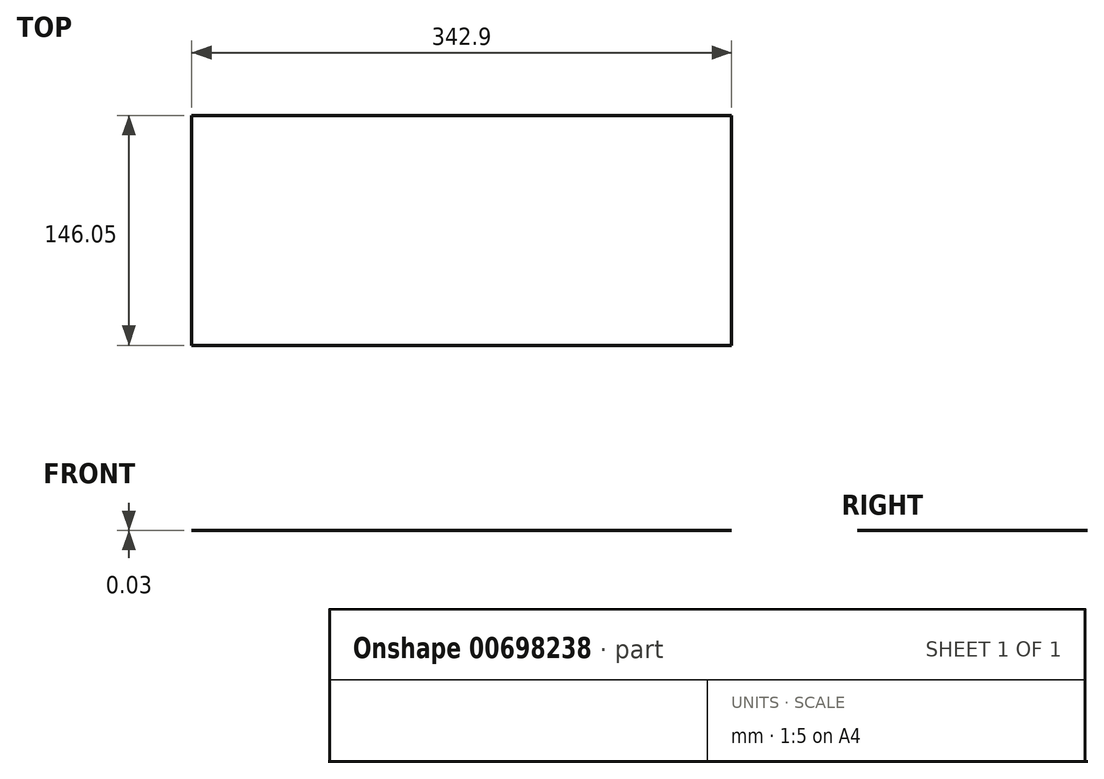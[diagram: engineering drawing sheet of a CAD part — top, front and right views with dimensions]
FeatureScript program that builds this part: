
annotation { "Feature Type Name" : "Feature", "Feature Type Description" : "" }
export const myFeature = defineFeature(function(context is Context, id is Id, definition is map)
    precondition{}
    {
        {
            var Q0;
            Q0=qCreatedBy(makeId("Top.planeOp"),FACE);
            var sketch = newSketch(context, id + "F0", { "sketchPlane" : qUnion([Q0])});
            skLineSegment(sketch, "E0.bottom", {"start": v(-162.15, -19.73) * mm, "end": v(180.75, -19.73) * mm});
            skLineSegment(sketch, "E0.top", {"start": v(-162.15, -165.78) * mm, "end": v(180.75, -165.78) * mm});
            skLineSegment(sketch, "E0.left", {"start": v(-162.15, -19.73) * mm, "end": v(-162.15, -165.78) * mm});
            skLineSegment(sketch, "E0.right", {"start": v(180.75, -19.73) * mm, "end": v(180.75, -165.78) * mm});
            skSolve(sketch);
        }
        {
            var Q0;
            Q0 = qSketchRegion(id + "F0", true);
            extrude(context, id + "F1", {"entities" : qUnion([Q0]), "depth" : 3 / 101.6 * mm, "offsetDistance" : 25.4 * mm});
        }
    });
